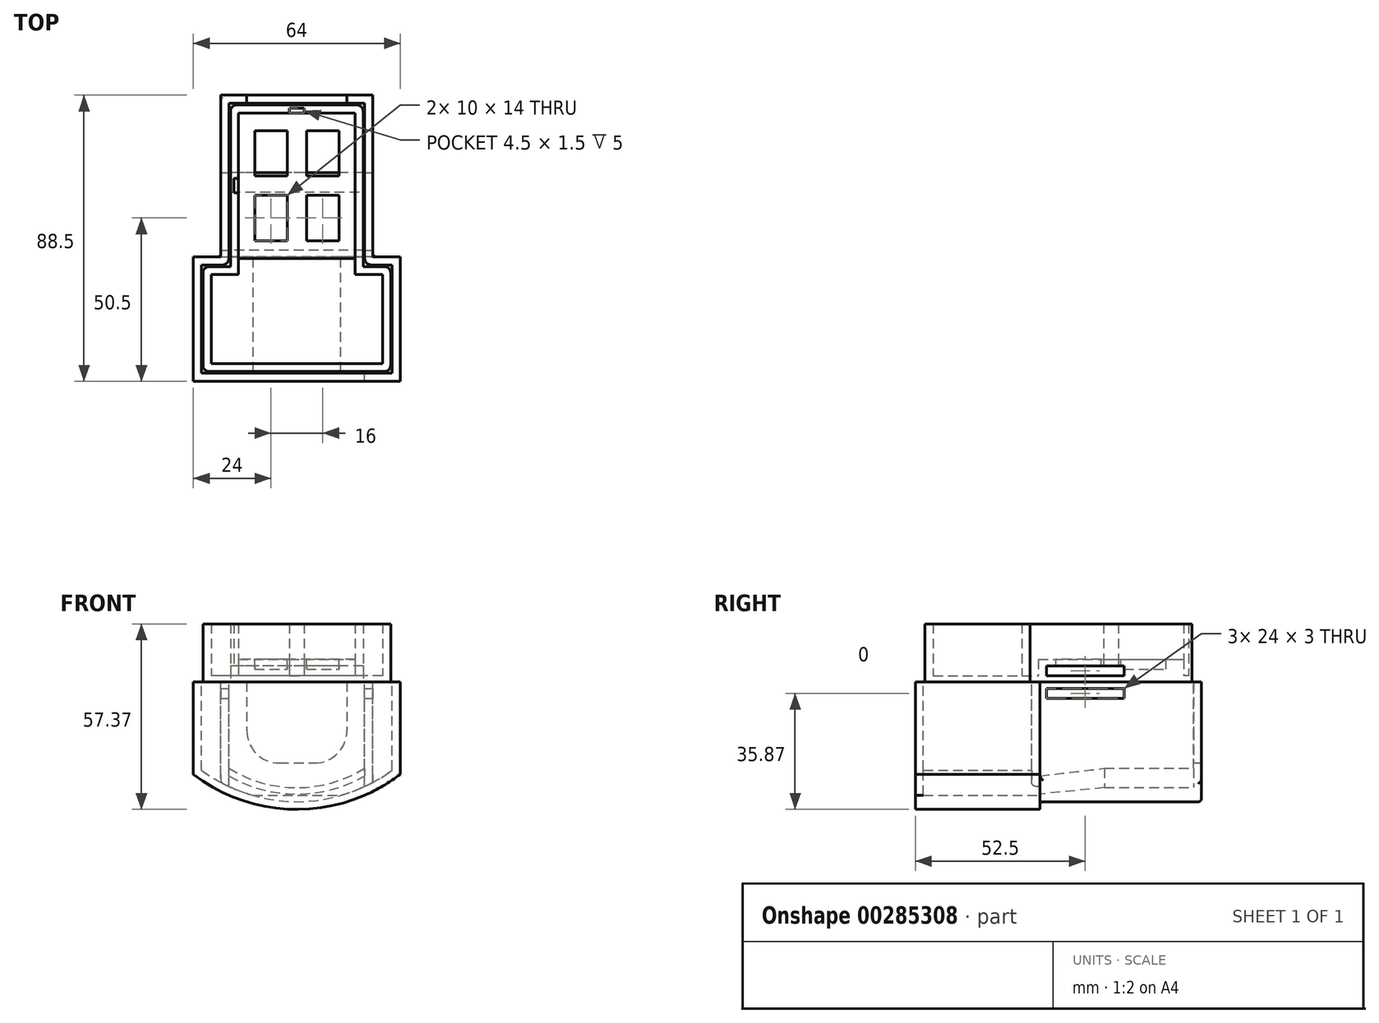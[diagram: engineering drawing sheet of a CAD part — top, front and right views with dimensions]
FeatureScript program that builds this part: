
annotation { "Feature Type Name" : "Feature", "Feature Type Description" : "" }
export const myFeature = defineFeature(function(context is Context, id is Id, definition is map)
    precondition{}
    {
        {
            var Q0;
            Q0=qCreatedBy(makeId("Top.planeOp"),FACE);
            var sketch = newSketch(context, id + "F0", { "sketchPlane" : qUnion([Q0])});
            skLineSegment(sketch, "E0.bottom", {"start": v(20.5, 25) * mm, "end": v(-20.5, 25) * mm});
            skLineSegment(sketch, "E0.left", {"start": v(20.5, 25) * mm, "end": v(20.5, -25) * mm});
            skLineSegment(sketch, "E0.right", {"start": v(-20.5, 25) * mm, "end": v(-20.5, -25) * mm});
            skPoint(sketch, "E0.middle", {"position": v(0, 0) * mm});
            skLineSegment(sketch, "E1.bottom", {"start": v(-29, -25) * mm, "end": v(-20.5, -25) * mm});
            skLineSegment(sketch, "E1.top", {"start": v(-29, -57.5) * mm, "end": v(29, -57.5) * mm});
            skLineSegment(sketch, "E1.left", {"start": v(-29, -25) * mm, "end": v(-29, -57.5) * mm});
            skLineSegment(sketch, "E1.right", {"start": v(29, -25) * mm, "end": v(29, -57.5) * mm});
            skPoint(sketch, "E1.middle", {"position": v(0, -41.25) * mm});
            skLineSegment(sketch, "E2.trimOffspring", {"start": v(20.5, -25) * mm, "end": v(29, -25) * mm});
            skLineSegment(sketch, "E3.0", {"start": v(18, 22.5) * mm, "end": v(2.25, 22.5) * mm});
            skLineSegment(sketch, "E3.1", {"start": v(-18, 22.5) * mm, "end": v(-18, 2.25) * mm});
            skLineSegment(sketch, "E3.2", {"start": v(18, 22.5) * mm, "end": v(18, -27.5) * mm});
            skLineSegment(sketch, "E3.3", {"start": v(-26.5, -27.5) * mm, "end": v(-18, -27.5) * mm});
            skLineSegment(sketch, "E3.4", {"start": v(18, -27.5) * mm, "end": v(26.5, -27.5) * mm});
            skLineSegment(sketch, "E3.5", {"start": v(26.5, -27.5) * mm, "end": v(26.5, -55) * mm});
            skLineSegment(sketch, "E3.6", {"start": v(-26.5, -55) * mm, "end": v(26.5, -55) * mm});
            skLineSegment(sketch, "E3.7", {"start": v(-26.5, -27.5) * mm, "end": v(-26.5, -55) * mm});
            skLineSegment(sketch, "E4.top", {"start": v(-2.25, 24) * mm, "end": v(2.25, 24) * mm});
            skLineSegment(sketch, "E4.left", {"start": v(-2.25, 22.5) * mm, "end": v(-2.25, 24) * mm});
            skLineSegment(sketch, "E4.right", {"start": v(2.25, 22.5) * mm, "end": v(2.25, 24) * mm});
            skLineSegment(sketch, "E5.trimOffspring", {"start": v(-2.25, 22.5) * mm, "end": v(-18, 22.5) * mm});
            skLineSegment(sketch, "E6.bottom", {"start": v(-18, 2.25) * mm, "end": v(-19.5, 2.25) * mm});
            skLineSegment(sketch, "E6.top", {"start": v(-18, -2.25) * mm, "end": v(-19.5, -2.25) * mm});
            skLineSegment(sketch, "E6.right", {"start": v(-19.5, 2.25) * mm, "end": v(-19.5, -2.25) * mm});
            skLineSegment(sketch, "E7.trimOffspring", {"start": v(-18, -2.25) * mm, "end": v(-18, -27.5) * mm});
            skLineSegment(sketch, "E8.0", {"start": v(-29.5, -24.5) * mm, "end": v(-29.5, -58) * mm});
            skLineSegment(sketch, "E8.1", {"start": v(-29.5, -24.5) * mm, "end": v(-23, -24.5) * mm});
            skLineSegment(sketch, "E8.2", {"start": v(-29.5, -58) * mm, "end": v(29.5, -58) * mm});
            skLineSegment(sketch, "E8.3", {"start": v(-21, 25.5) * mm, "end": v(-21, -22.5) * mm});
            skLineSegment(sketch, "E8.4", {"start": v(29.5, -24.5) * mm, "end": v(29.5, -58) * mm});
            skLineSegment(sketch, "E8.5", {"start": v(23, -24.5) * mm, "end": v(29.5, -24.5) * mm});
            skLineSegment(sketch, "E8.6", {"start": v(21, 25.5) * mm, "end": v(21, -22.5) * mm});
            skLineSegment(sketch, "E8.7", {"start": v(21, 25.5) * mm, "end": v(-21, 25.5) * mm});
            skLineSegment(sketch, "E9.0", {"start": v(-32, -22) * mm, "end": v(-32, -60.5) * mm});
            skLineSegment(sketch, "E9.1", {"start": v(-32, -22) * mm, "end": v(-23.5, -22) * mm});
            skLineSegment(sketch, "E9.2", {"start": v(-32, -60.5) * mm, "end": v(32, -60.5) * mm});
            skLineSegment(sketch, "E9.3", {"start": v(-23.5, 28) * mm, "end": v(-23.5, -22) * mm});
            skLineSegment(sketch, "E9.4", {"start": v(32, -22) * mm, "end": v(32, -60.5) * mm});
            skLineSegment(sketch, "E9.5", {"start": v(23.5, -22) * mm, "end": v(32, -22) * mm});
            skLineSegment(sketch, "E9.6", {"start": v(23.5, 28) * mm, "end": v(23.5, -22) * mm});
            skLineSegment(sketch, "E9.7", {"start": v(23.5, 28) * mm, "end": v(-23.5, 28) * mm});
            skPoint(sketch, "E10.visualSharp", {"position": v(-21, -24.5) * mm});
            skArc(sketch, "E10.filletArc", {"start": v(-23, -24.5) * mm, "mid": v(-21.59, -23.91) * mm, "end": v(-21, -22.5) * mm});
            skPoint(sketch, "E11.visualSharp", {"position": v(21, -24.5) * mm});
            skArc(sketch, "E11.filletArc", {"start": v(21, -22.5) * mm, "mid": v(21.59, -23.91) * mm, "end": v(23, -24.5) * mm});
            skSolve(sketch);
        }
        {
            var Q0;
            Q0=makeQuery(id+"F0.imprint","IMPRINT",FACE,{"disambiguationData":[TD([[makeQuery(id+"F0.imprint","IMPRINT",EDGE,{"derivedFrom":sQuery(id+"F0.wireOp",EDGE,"E0.bottom")}),1.0]])]});
            var Q1;
            Q1=makeQuery(id+"F0.imprint","IMPRINT",FACE,{"disambiguationData":[TD([[makeQuery(id+"F0.imprint","IMPRINT",EDGE,{"derivedFrom":sQuery(id+"F0.wireOp",EDGE,"E3.0")}),1.0]])]});
            extrude(context, id + "F1", {"entities" : qUnion([Q0, Q1]), "depth" : 2 * mm});
        }
        {
            var Q0;
            Q0=makeQuery(id+"F0.imprint","IMPRINT",FACE,{"disambiguationData":[TD([[makeQuery(id+"F0.imprint","IMPRINT",EDGE,{"derivedFrom":sQuery(id+"F0.wireOp",EDGE,"E0.bottom")}),1.0]])]});
            extrude(context, id + "F2", {"entities" : qUnion([Q0]), "operationType" : NewBodyOperationType.ADD, "depth" : 18 * mm});
        }
        {
            var Q0;
            Q0=makeQuery(id+"F1.opExtrude","CAP_FACE",FACE,{"disambiguationData":[OSD([sQuery(id+"F0.wireOp",EDGE,"E0.bottom"),sQuery(id+"F0.wireOp",EDGE,"E0.left"),sQuery(id+"F0.wireOp",EDGE,"E0.right"),sQuery(id+"F0.wireOp",EDGE,"E1.bottom"),sQuery(id+"F0.wireOp",EDGE,"E1.top"),sQuery(id+"F0.wireOp",EDGE,"E1.left"),sQuery(id+"F0.wireOp",EDGE,"E1.right"),sQuery(id+"F0.wireOp",EDGE,"E2.trimOffspring")])],"isStart":false});
            var sketch = newSketch(context, id + "F3", { "sketchPlane" : qUnion([Q0])});
            skLineSegment(sketch, "E12.bottom", {"start": v(18, 22.5) * mm, "end": v(-18, 22.5) * mm});
            skLineSegment(sketch, "E12.top", {"start": v(18, -22.5) * mm, "end": v(-18, -22.5) * mm});
            skLineSegment(sketch, "E12.left", {"start": v(18, 22.5) * mm, "end": v(18, -22.5) * mm});
            skLineSegment(sketch, "E12.right", {"start": v(-18, 22.5) * mm, "end": v(-18, -22.5) * mm});
            skPoint(sketch, "E12.middle", {"position": v(0, 0) * mm});
            skSolve(sketch);
        }
        {
            var Q0;
            {var subQ0=sQuery(id+"F3.wireOp",EDGE,"E12.top");Q0=makeQuery(id+"F3.imprint","IMPRINT",FACE,{"disambiguationData":[TD([[makeQuery(id+"F3.imprint","IMPRINT",EDGE,{"derivedFrom":subQ0}),-1.0]])]});}
            extrude(context, id + "F4", {"entities" : qUnion([Q0]), "operationType" : NewBodyOperationType.ADD, "depth" : 5 * mm});
        }
        {
            var Q0;
            {var subQ0=sQuery(id+"F0.wireOp",EDGE,"E0.right");Q0=makeQuery(id+"F2.boolean.opBoolean","MERGE",FACE,{"derivedFrom":[makeQuery(id+"F1.opExtrude","SWEPT_FACE",FACE,{"disambiguationData":[OSD([subQ0])]}),makeQuery(id+"F2.opExtrude","SWEPT_FACE",FACE,{"disambiguationData":[OSD([subQ0])]})]});}
            var sketch = newSketch(context, id + "F5", { "sketchPlane" : qUnion([Q0])});
            skLineSegment(sketch, "E13.bottom", {"start": v(20, 2) * mm, "end": v(-4, 2) * mm});
            skLineSegment(sketch, "E13.top", {"start": v(20, 5) * mm, "end": v(-4, 5) * mm});
            skLineSegment(sketch, "E13.left", {"start": v(20, 2) * mm, "end": v(20, 5) * mm});
            skLineSegment(sketch, "E14", {"start": v(-4, 5) * mm, "end": v(-4, 2) * mm});
            skSolve(sketch);
        }
        {
            var Q0;
            Q0=qSketchRegion(id+"F5",true);
            var Q1;
            {var subQ0=sQuery(id+"F0.wireOp",EDGE,"E0.left");Q1=makeQuery(id+"F2.boolean.opBoolean","MERGE",FACE,{"derivedFrom":[makeQuery(id+"F1.opExtrude","SWEPT_FACE",FACE,{"disambiguationData":[OSD([subQ0])]}),makeQuery(id+"F2.opExtrude","SWEPT_FACE",FACE,{"disambiguationData":[OSD([subQ0])]})]});}
            extrude(context, id + "F6", {"entities" : qUnion([Q0]), "operationType" : NewBodyOperationType.REMOVE, "endBound" : BoundingType.UP_TO_SURFACE, "oppositeDirection" : true, "endBoundEntityFace" : qUnion([Q1]), "depth" : 25 * mm});
        }
        {
            var Q0;
            Q0=makeQuery(id+"F4.opExtrude","CAP_FACE",FACE,{"disambiguationData":[OSD([sQuery(id+"F3.wireOp",EDGE,"E12.bottom"),sQuery(id+"F3.wireOp",EDGE,"E12.top"),sQuery(id+"F3.wireOp",EDGE,"E12.left"),sQuery(id+"F3.wireOp",EDGE,"E12.right")])],"isStart":false});
            var sketch = newSketch(context, id + "F7", { "sketchPlane" : qUnion([Q0])});
            skLineSegment(sketch, "E15.bottom", {"start": v(-3, 3) * mm, "end": v(-13, 3) * mm});
            skLineSegment(sketch, "E15.top", {"start": v(-3, 17) * mm, "end": v(-13, 17) * mm});
            skLineSegment(sketch, "E15.left", {"start": v(-3, 3) * mm, "end": v(-3, 17) * mm});
            skLineSegment(sketch, "E15.right", {"start": v(-13, 3) * mm, "end": v(-13, 17) * mm});
            skPoint(sketch, "E15.middle", {"position": v(-8, 10) * mm});
            skLineSegment(sketch, "E16.1.0.0", {"start": v(3, 3) * mm, "end": v(3, 17) * mm});
            skPoint(sketch, "E16.1.0.1", {"position": v(8, 10) * mm});
            skLineSegment(sketch, "E16.1.0.2", {"start": v(13, 3) * mm, "end": v(3, 3) * mm});
            skLineSegment(sketch, "E16.1.0.3", {"start": v(13, 3) * mm, "end": v(13, 17) * mm});
            skLineSegment(sketch, "E16.1.0.4", {"start": v(13, 17) * mm, "end": v(3, 17) * mm});
            skLineSegment(sketch, "E16.direction1", {"start": v(-13, 3) * mm, "end": v(3, 3) * mm, "construction": true});
            skLineSegment(sketch, "E17", {"start": v(-14.04, 0) * mm, "end": v(15.05, 0) * mm, "construction": true});
            skLineSegment(sketch, "E18.MirrorCS", {"start": v(-3, -3) * mm, "end": v(-13, -3) * mm});
            skLineSegment(sketch, "E19.MirrorCS", {"start": v(13, -3) * mm, "end": v(13, -17) * mm});
            skLineSegment(sketch, "E20.MirrorCS", {"start": v(-3, -3) * mm, "end": v(-3, -17) * mm});
            skPoint(sketch, "E21.MirrorP", {"position": v(-8, -10) * mm});
            skLineSegment(sketch, "E22.MirrorCS", {"start": v(13, -17) * mm, "end": v(3, -17) * mm});
            skLineSegment(sketch, "E23.MirrorCS", {"start": v(-13, -3) * mm, "end": v(3, -3) * mm, "construction": true});
            skLineSegment(sketch, "E24.MirrorCS", {"start": v(13, -3) * mm, "end": v(3, -3) * mm});
            skLineSegment(sketch, "E25.MirrorCS", {"start": v(3, -3) * mm, "end": v(3, -17) * mm});
            skLineSegment(sketch, "E26.MirrorCS", {"start": v(-13, -3) * mm, "end": v(-13, -17) * mm});
            skLineSegment(sketch, "E27.MirrorCS", {"start": v(-3, -17) * mm, "end": v(-13, -17) * mm});
            skPoint(sketch, "E28.MirrorP", {"position": v(8, -10) * mm});
            skSolve(sketch);
        }
        {
            var Q0;
            Q0=qSketchRegion(id+"F7",true);
            extrude(context, id + "F8", {"entities" : qUnion([Q0]), "operationType" : NewBodyOperationType.REMOVE, "oppositeDirection" : true, "depth" : 3 * mm});
        }
        {
            var Q0;
            Q0=makeQuery(id+"F0.imprint","IMPRINT",FACE,{"disambiguationData":[TD([[makeQuery(id+"F0.imprint","IMPRINT",EDGE,{"derivedFrom":sQuery(id+"F0.wireOp",EDGE,"E8.0")}),-1.0]])]});
            extrude(context, id + "F9", {"entities" : qUnion([Q0]), "oppositeDirection" : true, "depth" : 35 * mm});
        }
        {
            var Q0;
            Q0=makeQuery(id+"F9.opExtrude","CAP_FACE",FACE,{"disambiguationData":[OSD([sQuery(id+"F0.wireOp",EDGE,"E8.0"),sQuery(id+"F0.wireOp",EDGE,"E8.1"),sQuery(id+"F0.wireOp",EDGE,"E8.2"),sQuery(id+"F0.wireOp",EDGE,"E8.3"),sQuery(id+"F0.wireOp",EDGE,"E8.4"),sQuery(id+"F0.wireOp",EDGE,"E8.5"),sQuery(id+"F0.wireOp",EDGE,"E8.6"),sQuery(id+"F0.wireOp",EDGE,"E8.7"),sQuery(id+"F0.wireOp",EDGE,"E9.0"),sQuery(id+"F0.wireOp",EDGE,"E9.1"),sQuery(id+"F0.wireOp",EDGE,"E9.2"),sQuery(id+"F0.wireOp",EDGE,"E9.3"),sQuery(id+"F0.wireOp",EDGE,"E9.4"),sQuery(id+"F0.wireOp",EDGE,"E9.5"),sQuery(id+"F0.wireOp",EDGE,"E9.6"),sQuery(id+"F0.wireOp",EDGE,"E9.7"),sQuery(id+"F0.wireOp",EDGE,"E10.filletArc"),sQuery(id+"F0.wireOp",EDGE,"E11.filletArc")])],"isStart":false});
            var sketch = newSketch(context, id + "F10", { "sketchPlane" : qUnion([Q0])});
            skLineSegment(sketch, "E29.bottom", {"start": v(-32, 60.5) * mm, "end": v(32, 60.5) * mm});
            skLineSegment(sketch, "E29.top", {"start": v(-23.5, -28) * mm, "end": v(23.5, -28) * mm});
            skLineSegment(sketch, "E29.left", {"start": v(-32, 60.5) * mm, "end": v(-32, 22) * mm});
            skLineSegment(sketch, "E29.right", {"start": v(32, 60.5) * mm, "end": v(32, 22) * mm});
            skLineSegment(sketch, "E30", {"start": v(-32, 22) * mm, "end": v(-23.5, 22) * mm});
            skLineSegment(sketch, "E31", {"start": v(-23.5, 22) * mm, "end": v(-23.5, -28) * mm});
            skLineSegment(sketch, "E32", {"start": v(32, 22) * mm, "end": v(23.5, 22) * mm});
            skLineSegment(sketch, "E33", {"start": v(23.5, 22) * mm, "end": v(23.5, -28) * mm});
            skPoint(sketch, "E34.orphan", {"position": v(32, -28) * mm});
            skSolve(sketch);
        }
        {
            var Q0;
            Q0=qSketchRegion(id+"F10",true);
            extrude(context, id + "F11", {"entities" : qUnion([Q0]), "operationType" : NewBodyOperationType.ADD, "depth" : 2 * mm});
        }
        {
            var Q0;
            {var subQ0=sQuery(id+"F0.wireOp",EDGE,"E1.left");var subQ1=sQuery(id+"F0.wireOp",EDGE,"E1.top");Q0=makeQuery(id+"F2.boolean.opBoolean","MERGE",EDGE,{"derivedFrom":[makeQuery(id+"F1.opExtrude","SWEPT_EDGE",EDGE,{"disambiguationData":[OSD([subQ1,subQ0])]}),makeQuery(id+"F2.opExtrude","SWEPT_EDGE",EDGE,{"disambiguationData":[OSD([subQ1,subQ0])]})]});}
            var Q1;
            {var subQ0=sQuery(id+"F0.wireOp",EDGE,"E1.left");var subQ1=sQuery(id+"F0.wireOp",EDGE,"E1.bottom");Q1=makeQuery(id+"F2.boolean.opBoolean","MERGE",EDGE,{"derivedFrom":[makeQuery(id+"F1.opExtrude","SWEPT_EDGE",EDGE,{"disambiguationData":[OSD([subQ1,subQ0])]}),makeQuery(id+"F2.opExtrude","SWEPT_EDGE",EDGE,{"disambiguationData":[OSD([subQ1,subQ0])]})]});}
            var Q2;
            {var subQ0=sQuery(id+"F0.wireOp",EDGE,"E1.right");var subQ1=sQuery(id+"F0.wireOp",EDGE,"E1.top");Q2=makeQuery(id+"F2.boolean.opBoolean","MERGE",EDGE,{"derivedFrom":[makeQuery(id+"F1.opExtrude","SWEPT_EDGE",EDGE,{"disambiguationData":[OSD([subQ1,subQ0])]}),makeQuery(id+"F2.opExtrude","SWEPT_EDGE",EDGE,{"disambiguationData":[OSD([subQ1,subQ0])]})]});}
            var Q3;
            {var subQ0=sQuery(id+"F0.wireOp",EDGE,"E0.right");var subQ1=sQuery(id+"F0.wireOp",EDGE,"E0.bottom");Q3=makeQuery(id+"F2.boolean.opBoolean","MERGE",EDGE,{"derivedFrom":[makeQuery(id+"F1.opExtrude","SWEPT_EDGE",EDGE,{"disambiguationData":[OSD([subQ1,subQ0])]}),makeQuery(id+"F2.opExtrude","SWEPT_EDGE",EDGE,{"disambiguationData":[OSD([subQ1,subQ0])]})]});}
            var Q4;
            {var subQ0=sQuery(id+"F0.wireOp",EDGE,"E2.trimOffspring");var subQ1=sQuery(id+"F0.wireOp",EDGE,"E1.right");Q4=makeQuery(id+"F2.boolean.opBoolean","MERGE",EDGE,{"derivedFrom":[makeQuery(id+"F1.opExtrude","SWEPT_EDGE",EDGE,{"disambiguationData":[OSD([subQ1,subQ0])]}),makeQuery(id+"F2.opExtrude","SWEPT_EDGE",EDGE,{"disambiguationData":[OSD([subQ1,subQ0])]})]});}
            var Q5;
            {var subQ0=sQuery(id+"F0.wireOp",EDGE,"E0.left");var subQ1=sQuery(id+"F0.wireOp",EDGE,"E0.bottom");Q5=makeQuery(id+"F2.boolean.opBoolean","MERGE",EDGE,{"derivedFrom":[makeQuery(id+"F1.opExtrude","SWEPT_EDGE",EDGE,{"disambiguationData":[OSD([subQ1,subQ0])]}),makeQuery(id+"F2.opExtrude","SWEPT_EDGE",EDGE,{"disambiguationData":[OSD([subQ1,subQ0])]})]});}
            fillet(context, id + "F12", {"entities" : qUnion([Q0, Q1, Q2, Q3, Q4, Q5]), "radius" : 2 * mm, "tangentPropagation" : true, "allowEdgeOverflow" : false});
        }
        {
            var Q0;
            Q0=makeQuery(id+"F11.boolean.opBoolean","MERGE",FACE,{"derivedFrom":[makeQuery(id+"F9.opExtrude","SWEPT_FACE",FACE,{"disambiguationData":[OSD([sQuery(id+"F0.wireOp",EDGE,"E9.7")])]}),makeQuery(id+"F11.opExtrude","SWEPT_FACE",FACE,{"disambiguationData":[OSD([sQuery(id+"F10.wireOp",EDGE,"E29.top")])]})]});
            var sketch = newSketch(context, id + "F13", { "sketchPlane" : qUnion([Q0])});
            skLineSegment(sketch, "E35.top", {"start": v(-15.5, 0) * mm, "end": v(15.5, 0) * mm});
            skLineSegment(sketch, "E35.left", {"start": v(-15.5, -25) * mm, "end": v(-15.5, 0) * mm});
            skLineSegment(sketch, "E35.right", {"start": v(15.5, -25) * mm, "end": v(15.5, 0) * mm});
            skLineSegment(sketch, "E36", {"start": v(-15.5, -25) * mm, "end": v(15.5, -25) * mm});
            skSolve(sketch);
        }
        {
            var Q0;
            Q0=qSketchRegion(id+"F13",true);
            var Q1;
            Q1=makeQuery(id+"F9.opExtrude","SWEPT_FACE",FACE,{"disambiguationData":[OSD([sQuery(id+"F0.wireOp",EDGE,"E8.7")])]});
            extrude(context, id + "F14", {"entities" : qUnion([Q0]), "operationType" : NewBodyOperationType.REMOVE, "endBound" : BoundingType.UP_TO_SURFACE, "oppositeDirection" : true, "endBoundEntityFace" : qUnion([Q1]), "depth" : 25 * mm});
        }
        {
            var Q0;
            Q0=makeQuery(id+"F14.boolean.opBoolean","COPY",EDGE,{"derivedFrom":makeQuery(id+"F14.opExtrude","SWEPT_EDGE",EDGE,{"disambiguationData":[OSD([sQuery(id+"F13.wireOp",EDGE,"E35.left"),sQuery(id+"F13.wireOp",EDGE,"E36")])]})});
            var Q1;
            Q1=makeQuery(id+"F14.boolean.opBoolean","COPY",EDGE,{"derivedFrom":makeQuery(id+"F14.opExtrude","SWEPT_EDGE",EDGE,{"disambiguationData":[OSD([sQuery(id+"F13.wireOp",EDGE,"E35.right"),sQuery(id+"F13.wireOp",EDGE,"E36")])]})});
            fillet(context, id + "F15", {"entities" : qUnion([Q0, Q1]), "radius" : 10 * mm, "tangentPropagation" : true, "allowEdgeOverflow" : false});
        }
        {
            var Q0;
            Q0=makeQuery(id+"F11.boolean.opBoolean","MERGE",FACE,{"derivedFrom":[makeQuery(id+"F9.opExtrude","SWEPT_FACE",FACE,{"disambiguationData":[OSD([sQuery(id+"F0.wireOp",EDGE,"E9.7")])]}),makeQuery(id+"F11.opExtrude","SWEPT_FACE",FACE,{"disambiguationData":[OSD([sQuery(id+"F10.wireOp",EDGE,"E29.top")])]})]});
            var sketch = newSketch(context, id + "F16", { "sketchPlane" : qUnion([Q0])});
            skArc(sketch, "E37", {"start": v(-23.5, -25) * mm, "mid": v(0, -32.63) * mm, "end": v(23.5, -25) * mm});
            skPoint(sketch, "E37.first.point", {"position": v(-23.5, -25) * mm});
            skPoint(sketch, "E37.second.point", {"position": v(23.5, -25) * mm});
            skPoint(sketch, "E37.third.point", {"position": v(0, -32.63) * mm});
            skPoint(sketch, "E37.third.point.positionSnap0", {"position": v(0, -25) * mm});
            skArc(sketch, "E38", {"start": v(-23.5, -31) * mm, "mid": v(0, -37) * mm, "end": v(23.5, -31) * mm});
            skPoint(sketch, "E38.first.point", {"position": v(-23.5, -31) * mm});
            skPoint(sketch, "E38.second.point", {"position": v(23.5, -31) * mm});
            skArc(sketch, "E39", {"start": v(-23.5, -37.7) * mm, "mid": v(0, -42.98) * mm, "end": v(23.5, -37.7) * mm});
            skLineSegment(sketch, "E40", {"start": v(-23.5, -25) * mm, "end": v(-23.5, -37.7) * mm});
            skLineSegment(sketch, "E41", {"start": v(23.5, -25) * mm, "end": v(23.5, -37.7) * mm});
            skSolve(sketch);
        }
        {
            var Q0;
            {var subQ4=sQuery(id+"F16.wireOp",EDGE,"E39");Q0=makeQuery(id+"F16.imprint","IMPRINT",FACE,{"disambiguationData":[TD([[makeQuery(id+"F16.imprint","IMPRINT",EDGE,{"derivedFrom":subQ4}),1.0]])]});}
            var Q1;
            {var subQ0=sQuery(id+"F16.wireOp",EDGE,"E40");var subQ1=sQuery(id+"F16.wireOp",EDGE,"E38");var subQ2=makeQuery(id+"F16.imprint","INTERSECT",VERTEX,{"derivedFrom":[subQ1,subQ0]});Q1=makeQuery(id+"F16.imprint","IMPRINT",FACE,{"disambiguationData":[TD([[makeQuery(id+"F16.imprint","IMPRINT",EDGE,{"disambiguationData":[TD([[subQ2,-1.0]])],"derivedFrom":subQ1}),-1.0]])]});}
            var Q2;
            {var subQ0=sQuery(id+"F16.wireOp",EDGE,"E41");var subQ1=sQuery(id+"F16.wireOp",EDGE,"E38");var subQ2=makeQuery(id+"F16.imprint","INTERSECT",VERTEX,{"derivedFrom":[subQ1,subQ0]});Q2=makeQuery(id+"F16.imprint","IMPRINT",FACE,{"disambiguationData":[TD([[makeQuery(id+"F16.imprint","IMPRINT",EDGE,{"disambiguationData":[TD([[subQ2,1.0]])],"derivedFrom":subQ1}),-1.0]])]});}
            var Q3;
            Q3=makeQuery(id+"F11.boolean.opBoolean","MERGE",FACE,{"derivedFrom":[makeQuery(id+"F9.opExtrude","SWEPT_FACE",FACE,{"disambiguationData":[OSD([sQuery(id+"F0.wireOp",EDGE,"E9.5")])]}),makeQuery(id+"F11.opExtrude","SWEPT_FACE",FACE,{"disambiguationData":[OSD([sQuery(id+"F10.wireOp",EDGE,"E32")])]})]});
            extrude(context, id + "F17", {"entities" : qUnion([Q0, Q1, Q2]), "operationType" : NewBodyOperationType.REMOVE, "endBound" : BoundingType.UP_TO_SURFACE, "oppositeDirection" : true, "endBoundEntityFace" : qUnion([Q3]), "depth" : 25 * mm});
        }
        {
            var Q0;
            {var subQ1=sQuery(id+"F16.wireOp",EDGE,"E37");Q0=makeQuery(id+"F16.imprint","IMPRINT",FACE,{"disambiguationData":[TD([[makeQuery(id+"F16.imprint","IMPRINT",EDGE,{"derivedFrom":subQ1}),-1.0]])]});}
            var Q1;
            {var subQ0=sQuery(id+"F16.wireOp",EDGE,"E38");var subQ1=sQuery(id+"F10.wireOp",EDGE,"E29.top");var subQ2=makeQuery(id+"FvyC7EhlZyNcf0s_2.opFillet","BLEND_EDGE",EDGE,{"blendedFrom":[makeQuery(id+"F11.opExtrude","CAP_EDGE",EDGE,{"disambiguationData":[OSD([subQ1])],"isStart":false}),makeQuery(id+"F11.boolean.opBoolean","MERGE",FACE,{"derivedFrom":[makeQuery(id+"F9.opExtrude","SWEPT_FACE",FACE,{"disambiguationData":[OSD([sQuery(id+"F0.wireOp",EDGE,"E9.7")])]}),makeQuery(id+"F11.opExtrude","SWEPT_FACE",FACE,{"disambiguationData":[OSD([subQ1])]})]})],"blendedInto":[makeQuery(id+"F11.boolean.opBoolean","MERGE",FACE,{"derivedFrom":[makeQuery(id+"F9.opExtrude","SWEPT_FACE",FACE,{"disambiguationData":[OSD([sQuery(id+"F0.wireOp",EDGE,"E9.7")])]}),makeQuery(id+"F11.opExtrude","SWEPT_FACE",FACE,{"disambiguationData":[OSD([subQ1])]})]})]});var subQ3=makeQuery(id+"F16.imprint","INTERSECT",VERTEX,{"disambiguationData":[OD(0.0)],"derivedFrom":[subQ2,subQ0]});Q1=makeQuery(id+"F16.imprint","IMPRINT",FACE,{"disambiguationData":[TD([[makeQuery(id+"F16.imprint","IMPRINT",EDGE,{"disambiguationData":[TD([[subQ3,-1.0]])],"derivedFrom":subQ0}),1.0]])]});}
            var Q2;
            Q2=makeQuery(id+"F17.boolean.opBoolean","MERGE",FACE,{"derivedFrom":[makeQuery(id+"F11.boolean.opBoolean","MERGE",FACE,{"derivedFrom":[makeQuery(id+"F9.opExtrude","SWEPT_FACE",FACE,{"disambiguationData":[OSD([sQuery(id+"F0.wireOp",EDGE,"E9.1")])]}),makeQuery(id+"F11.opExtrude","SWEPT_FACE",FACE,{"disambiguationData":[OSD([sQuery(id+"F10.wireOp",EDGE,"E30")])]})]})],"fromTools":[makeQuery(id+"F17.opExtrude","CAP_FACE",FACE,{"disambiguationData":[OSD([sQuery(id+"F16.wireOp",EDGE,"E38"),sQuery(id+"F16.wireOp",EDGE,"E39"),sQuery(id+"F16.wireOp",EDGE,"E40"),sQuery(id+"F16.wireOp",EDGE,"E41")])],"isStart":false})]});
            extrude(context, id + "F18", {"entities" : qUnion([Q0, Q1]), "operationType" : NewBodyOperationType.ADD, "endBound" : BoundingType.UP_TO_SURFACE, "oppositeDirection" : true, "endBoundEntityFace" : qUnion([Q2]), "depth" : 25 * mm});
        }
        {
            var Q0;
            Q0=makeQuery(id+"F17.boolean.opBoolean","MERGE",FACE,{"derivedFrom":[makeQuery(id+"F11.boolean.opBoolean","MERGE",FACE,{"derivedFrom":[makeQuery(id+"F9.opExtrude","SWEPT_FACE",FACE,{"disambiguationData":[OSD([sQuery(id+"F0.wireOp",EDGE,"E9.5")])]}),makeQuery(id+"F11.opExtrude","SWEPT_FACE",FACE,{"disambiguationData":[OSD([sQuery(id+"F10.wireOp",EDGE,"E32")])]})]})],"fromTools":[makeQuery(id+"F17.opExtrude","CAP_FACE",FACE,{"disambiguationData":[OSD([sQuery(id+"F16.wireOp",EDGE,"E38"),sQuery(id+"F16.wireOp",EDGE,"E39"),sQuery(id+"F16.wireOp",EDGE,"E40"),sQuery(id+"F16.wireOp",EDGE,"E41")])],"isStart":false})]});
            var sketch = newSketch(context, id + "F19", { "sketchPlane" : qUnion([Q0])});
            skArc(sketch, "E42", {"start": v(-32, -25.29) * mm, "mid": v(0, -36.87) * mm, "end": v(32, -25.29) * mm});
            skPoint(sketch, "E42.first.point", {"position": v(-23.5, -31) * mm});
            skPoint(sketch, "E42.second.point", {"position": v(23.5, -31) * mm});
            skArc(sketch, "E43", {"start": v(-32, -37.62) * mm, "mid": v(0, -46.87) * mm, "end": v(32, -37.62) * mm});
            skArc(sketch, "E44", {"start": v(-32, -28.49) * mm, "mid": v(0, -39.37) * mm, "end": v(32, -28.49) * mm});
            skLineSegment(sketch, "E45", {"start": v(-32, -25.29) * mm, "end": v(-32, -37.62) * mm});
            skLineSegment(sketch, "E46", {"start": v(32, -25.29) * mm, "end": v(32, -37.62) * mm});
            skSolve(sketch);
        }
        {
            var Q0;
            {var subQ0=sQuery(id+"F19.wireOp",EDGE,"E45");var subQ6=sQuery(id+"F19.wireOp",EDGE,"E44");var subQ7=makeQuery(id+"F19.imprint","INTERSECT",VERTEX,{"derivedFrom":[subQ6,subQ0]});Q0=makeQuery(id+"F19.imprint","IMPRINT",FACE,{"disambiguationData":[TD([[makeQuery(id+"F19.imprint","IMPRINT",EDGE,{"disambiguationData":[TD([[subQ7,-1.0]])],"derivedFrom":subQ6}),-1.0]])]});}
            var Q1;
            {var subQ0=sQuery(id+"F19.wireOp",EDGE,"E46");var subQ1=sQuery(id+"F19.wireOp",EDGE,"E43");var subQ2=makeQuery(id+"F19.imprint","INTERSECT",VERTEX,{"derivedFrom":[subQ1,subQ0]});Q1=makeQuery(id+"F19.imprint","IMPRINT",FACE,{"disambiguationData":[TD([[makeQuery(id+"F19.imprint","IMPRINT",EDGE,{"disambiguationData":[TD([[subQ2,1.0]])],"derivedFrom":subQ0}),-1.0]])]});}
            var Q2;
            {var subQ12=sQuery(id+"F19.wireOp",EDGE,"E45");var subQ15=sQuery(id+"F19.wireOp",EDGE,"E44");var subQ16=makeQuery(id+"F19.imprint","INTERSECT",VERTEX,{"derivedFrom":[subQ15,subQ12]});Q2=makeQuery(id+"F19.imprint","IMPRINT",FACE,{"disambiguationData":[TD([[makeQuery(id+"F19.imprint","IMPRINT",EDGE,{"disambiguationData":[TD([[subQ16,-1.0]])],"derivedFrom":subQ15}),1.0]])]});}
            var Q3;
            {var subQ1=makeQuery(id+"F9.opExtrude","SWEPT_FACE",FACE,{"disambiguationData":[OSD([sQuery(id+"F0.wireOp",EDGE,"E9.5")])]});var subQ2=sQuery(id+"F16.wireOp",EDGE,"E38");var subQ3=makeQuery(id+"F17.opExtrude","CAP_FACE",FACE,{"disambiguationData":[OSD([subQ2,sQuery(id+"F16.wireOp",EDGE,"E39"),sQuery(id+"F16.wireOp",EDGE,"E40"),sQuery(id+"F16.wireOp",EDGE,"E41")])],"isStart":false});var subQ5=sQuery(id+"F10.wireOp",EDGE,"E32");var subQ13=makeQuery(id+"F11.opExtrude","SWEPT_FACE",FACE,{"disambiguationData":[OSD([subQ5])]});var subQ19=makeQuery(id+"F17.opExtrude","SWEPT_FACE",FACE,{"disambiguationData":[OSD([subQ2])]});var subQ20=makeQuery(id+"F17.boolean.opBoolean","COPY",EDGE,{"disambiguationData":[topologyDisambiguationEdgeConnected([subQ1,subQ13,subQ19,subQ3]),TD([makeQuery(id+"F9.opExtrude","SWEPT_FACE",FACE,{"disambiguationData":[OSD([sQuery(id+"F0.wireOp",EDGE,"E9.1")])]})])],"derivedFrom":makeQuery(id+"F17.opExtrude","CAP_EDGE",EDGE,{"disambiguationData":[OSD([subQ2])],"isStart":false})});Q3=makeQuery(id+"F19.imprint","IMPRINT",FACE,{"disambiguationData":[TD([[makeQuery(id+"F19.imprint","IMPRINT",EDGE,{"derivedFrom":subQ20}),-1.0]])]});}
            var Q4;
            {var subQ0=sQuery(id+"F19.wireOp",EDGE,"E46");var subQ18=sQuery(id+"F19.wireOp",EDGE,"E42");var subQ19=makeQuery(id+"F19.imprint","INTERSECT",VERTEX,{"derivedFrom":[subQ18,subQ0]});Q4=makeQuery(id+"F19.imprint","IMPRINT",FACE,{"disambiguationData":[TD([[makeQuery(id+"F19.imprint","IMPRINT",EDGE,{"disambiguationData":[TD([[subQ19,-1.0]])],"derivedFrom":subQ0}),-1.0]])]});}
            var Q5;
            Q5=makeQuery(id+"F11.boolean.opBoolean","MERGE",FACE,{"derivedFrom":[makeQuery(id+"F9.opExtrude","SWEPT_FACE",FACE,{"disambiguationData":[OSD([sQuery(id+"F0.wireOp",EDGE,"E9.2")])]}),makeQuery(id+"F11.opExtrude","SWEPT_FACE",FACE,{"disambiguationData":[OSD([sQuery(id+"F10.wireOp",EDGE,"E29.bottom")])]})]});
            extrude(context, id + "F20", {"entities" : qUnion([Q0, Q1, Q2, Q3, Q4]), "operationType" : NewBodyOperationType.REMOVE, "endBound" : BoundingType.UP_TO_SURFACE, "oppositeDirection" : true, "endBoundEntityFace" : qUnion([Q5]), "depth" : 25 * mm});
        }
        {
            var Q0;
            {var subQ15=sQuery(id+"F19.wireOp",EDGE,"E45");var subQ18=sQuery(id+"F19.wireOp",EDGE,"E44");var subQ19=makeQuery(id+"F19.imprint","INTERSECT",VERTEX,{"derivedFrom":[subQ18,subQ15]});Q0=makeQuery(id+"F19.imprint","IMPRINT",FACE,{"disambiguationData":[TD([[makeQuery(id+"F19.imprint","IMPRINT",EDGE,{"disambiguationData":[TD([[subQ19,-1.0]])],"derivedFrom":subQ18}),1.0]])]});}
            var Q1;
            {var subQ1=makeQuery(id+"F9.opExtrude","SWEPT_FACE",FACE,{"disambiguationData":[OSD([sQuery(id+"F0.wireOp",EDGE,"E9.5")])]});var subQ2=sQuery(id+"F16.wireOp",EDGE,"E38");var subQ3=makeQuery(id+"F17.opExtrude","CAP_FACE",FACE,{"disambiguationData":[OSD([subQ2,sQuery(id+"F16.wireOp",EDGE,"E39"),sQuery(id+"F16.wireOp",EDGE,"E40"),sQuery(id+"F16.wireOp",EDGE,"E41")])],"isStart":false});var subQ5=sQuery(id+"F10.wireOp",EDGE,"E32");var subQ13=makeQuery(id+"F11.opExtrude","SWEPT_FACE",FACE,{"disambiguationData":[OSD([subQ5])]});var subQ19=makeQuery(id+"F17.opExtrude","SWEPT_FACE",FACE,{"disambiguationData":[OSD([subQ2])]});var subQ20=makeQuery(id+"F17.boolean.opBoolean","COPY",EDGE,{"disambiguationData":[topologyDisambiguationEdgeConnected([subQ1,subQ13,subQ19,subQ3]),TD([makeQuery(id+"F9.opExtrude","SWEPT_FACE",FACE,{"disambiguationData":[OSD([sQuery(id+"F0.wireOp",EDGE,"E9.1")])]})])],"derivedFrom":makeQuery(id+"F17.opExtrude","CAP_EDGE",EDGE,{"disambiguationData":[OSD([subQ2])],"isStart":false})});Q1=makeQuery(id+"F19.imprint","IMPRINT",FACE,{"disambiguationData":[TD([[makeQuery(id+"F19.imprint","IMPRINT",EDGE,{"derivedFrom":subQ20}),-1.0]])]});}
            var Q2;
            {var subQ0=sQuery(id+"F19.wireOp",EDGE,"E46");var subQ1=sQuery(id+"F19.wireOp",EDGE,"E42");var subQ2=makeQuery(id+"F19.imprint","INTERSECT",VERTEX,{"derivedFrom":[subQ1,subQ0]});Q2=makeQuery(id+"F19.imprint","IMPRINT",FACE,{"disambiguationData":[TD([[makeQuery(id+"F19.imprint","IMPRINT",EDGE,{"disambiguationData":[TD([[subQ2,-1.0]])],"derivedFrom":subQ0}),-1.0]])]});}
            var Q3;
            Q3=makeQuery(id+"F11.boolean.opBoolean","MERGE",FACE,{"derivedFrom":[makeQuery(id+"F9.opExtrude","SWEPT_FACE",FACE,{"disambiguationData":[OSD([sQuery(id+"F0.wireOp",EDGE,"E9.2")])]}),makeQuery(id+"F11.opExtrude","SWEPT_FACE",FACE,{"disambiguationData":[OSD([sQuery(id+"F10.wireOp",EDGE,"E29.bottom")])]})]});
            extrude(context, id + "F21", {"entities" : qUnion([Q0, Q1, Q2]), "operationType" : NewBodyOperationType.ADD, "endBound" : BoundingType.UP_TO_SURFACE, "oppositeDirection" : true, "endBoundEntityFace" : qUnion([Q3]), "depth" : 25 * mm});
        }
        {
            var Q0;
            {var subQ0=sQuery(id+"F19.wireOp",EDGE,"E44");var subQ1=sQuery(id+"F10.wireOp",EDGE,"E33");var subQ2=sQuery(id+"F10.wireOp",EDGE,"E32");var subQ3=sQuery(id+"F10.wireOp",EDGE,"E31");var subQ4=sQuery(id+"F10.wireOp",EDGE,"E30");var subQ5=sQuery(id+"F10.wireOp",EDGE,"E29.right");var subQ6=sQuery(id+"F10.wireOp",EDGE,"E29.left");var subQ7=sQuery(id+"F10.wireOp",EDGE,"E29.top");var subQ8=sQuery(id+"F10.wireOp",EDGE,"E29.bottom");var subQ9=makeQuery(id+"F11.opExtrude","CAP_FACE",FACE,{"disambiguationData":[OSD([subQ8,subQ7,subQ6,subQ5,subQ4,subQ3,subQ2,subQ1])],"isStart":true});var subQ13=sQuery(id+"F0.wireOp",EDGE,"E9.5");var subQ14=makeQuery(id+"F17.opExtrude","CAP_FACE",FACE,{"disambiguationData":[OSD([subQ13,subQ2])],"isStart":false});var subQ15=makeQuery(id+"F9.opExtrude","SWEPT_FACE",FACE,{"disambiguationData":[OSD([subQ13])]});var subQ18=makeQuery(id+"F20.opExtrude","SWEPT_FACE",FACE,{"disambiguationData":[OSD([subQ0]),TDD([makeQuery(id+"F19.imprint","IMPRINT",EDGE,{"disambiguationData":[TD([[makeQuery(id+"F19.imprint","INTERSECT",VERTEX,{"derivedFrom":[makeQuery(id+"F17.boolean.opBoolean","INTERSECT",EDGE,{"disambiguationData":[topologyDisambiguationEdgeConnected([subQ15])],"derivedFrom":[subQ9,subQ14]}),subQ0]}),-1.0]])],"derivedFrom":subQ0}),makeQuery(id+"F19.imprint","IMPRINT",EDGE,{"disambiguationData":[TD([[makeQuery(id+"F19.imprint","INTERSECT",VERTEX,{"derivedFrom":[subQ0,sQuery(id+"F19.wireOp",EDGE,"E46")]}),1.0]])],"derivedFrom":subQ0})])]});Q0=makeQuery(id+"F21.boolean.opBoolean","MERGE",FACE,{"derivedFrom":[makeQuery(id+"F20.boolean.opBoolean","COPY",FACE,{"derivedFrom":makeQuery(id+"F20.opExtrude","SWEPT_FACE",FACE,{"disambiguationData":[OSD([subQ0]),TDD([makeQuery(id+"F19.imprint","IMPRINT",EDGE,{"disambiguationData":[TD([[makeQuery(id+"F19.imprint","INTERSECT",VERTEX,{"derivedFrom":[subQ0,sQuery(id+"F19.wireOp",EDGE,"E45")]}),-1.0]])],"derivedFrom":subQ0})])]})}),makeQuery(id+"F20.boolean.opBoolean","COPY",FACE,{"disambiguationData":[TD([subQ15])],"derivedFrom":subQ18}),makeQuery(id+"F20.boolean.opBoolean","COPY",FACE,{"disambiguationData":[TD([makeQuery(id+"F9.opExtrude","SWEPT_FACE",FACE,{"disambiguationData":[OSD([sQuery(id+"F0.wireOp",EDGE,"E8.0")])]})])],"derivedFrom":subQ18}),makeQuery(id+"F21.opExtrude","SWEPT_FACE",FACE,{"disambiguationData":[OSD([subQ0])]})]});}
            var Q1;
            {var subQ0=sQuery(id+"F16.wireOp",EDGE,"E38");Q1=makeQuery(id+"F18.boolean.opBoolean","MERGE",FACE,{"derivedFrom":[makeQuery(id+"F17.boolean.opBoolean","COPY",FACE,{"derivedFrom":makeQuery(id+"F17.opExtrude","SWEPT_FACE",FACE,{"disambiguationData":[OSD([subQ0])]})}),makeQuery(id+"F18.opExtrude","SWEPT_FACE",FACE,{"disambiguationData":[OSD([subQ0])]})]});}
            fillet(context, id + "F22", {"entities" : qUnion([Q0, Q1]), "radius" : 1 * mm, "tangentPropagation" : true, "allowEdgeOverflow" : false});
        }
        {
            var Q0;
            Q0=makeQuery(id+"F11.boolean.opBoolean","MERGE",FACE,{"derivedFrom":[makeQuery(id+"F9.opExtrude","SWEPT_FACE",FACE,{"disambiguationData":[OSD([sQuery(id+"F0.wireOp",EDGE,"E9.6")])]}),makeQuery(id+"F11.opExtrude","SWEPT_FACE",FACE,{"disambiguationData":[OSD([sQuery(id+"F10.wireOp",EDGE,"E33")])]})]});
            var sketch = newSketch(context, id + "F23", { "sketchPlane" : qUnion([Q0])});
            skLineSegment(sketch, "E47.bottom", {"start": v(-20, -2) * mm, "end": v(4, -2) * mm});
            skLineSegment(sketch, "E47.top", {"start": v(-20, -5) * mm, "end": v(4, -5) * mm});
            skLineSegment(sketch, "E47.left", {"start": v(-20, -2) * mm, "end": v(-20, -5) * mm});
            skLineSegment(sketch, "E47.right", {"start": v(4, -2) * mm, "end": v(4, -5) * mm});
            skSolve(sketch);
        }
        {
            var Q0;
            Q0 = qSketchRegion(id + "F23", true);
            var Q1;
            Q1=makeQuery(id+"F11.boolean.opBoolean","MERGE",FACE,{"derivedFrom":[makeQuery(id+"F9.opExtrude","SWEPT_FACE",FACE,{"disambiguationData":[OSD([sQuery(id+"F0.wireOp",EDGE,"E9.3")])]}),makeQuery(id+"F11.opExtrude","SWEPT_FACE",FACE,{"disambiguationData":[OSD([sQuery(id+"F10.wireOp",EDGE,"E31")])]})]});
            extrude(context, id + "F24", {"entities" : qUnion([Q0]), "operationType" : NewBodyOperationType.REMOVE, "endBound" : BoundingType.UP_TO_SURFACE, "oppositeDirection" : true, "endBoundEntityFace" : qUnion([Q1]), "depth" : 25 * mm});
        }
        {
            var Q0;
            Q0=makeQuery(id+"F18.opExtrude","CAP_EDGE",EDGE,{"disambiguationData":[OSD([sQuery(id+"F16.wireOp",EDGE,"E37")])],"isStart":false});
            chamfer(context, id + "F25", {"entities" : qUnion([Q0]), "chamferType" : ChamferType.TWO_OFFSETS, "width1" : 2 * mm, "oppositeDirection" : false, "width2" : 20 * mm, "tangentPropagation" : true});
        }
    });
